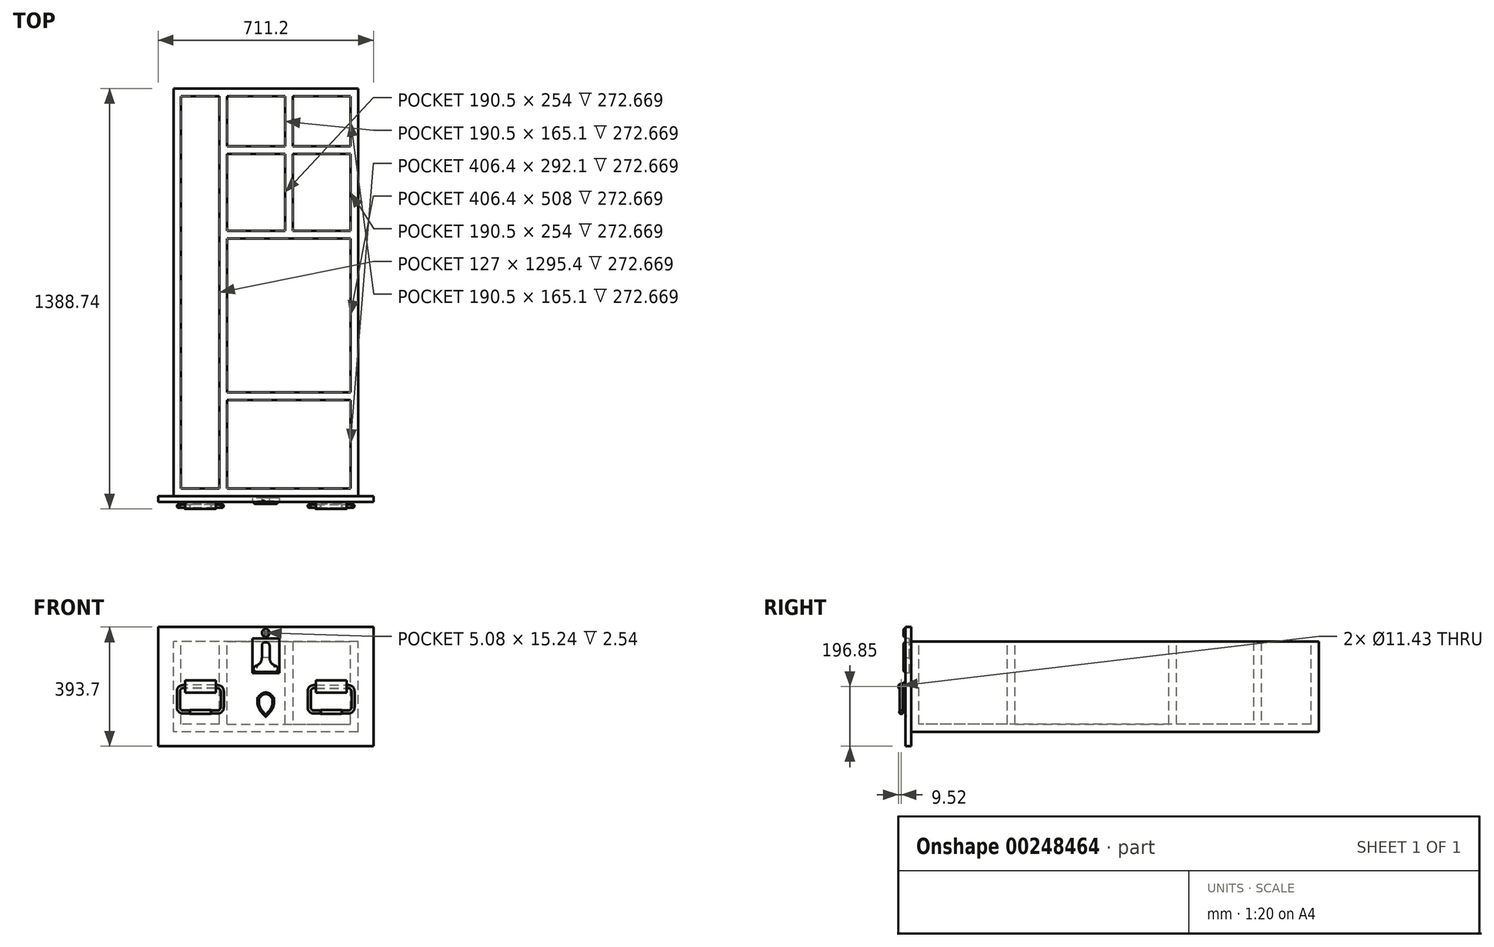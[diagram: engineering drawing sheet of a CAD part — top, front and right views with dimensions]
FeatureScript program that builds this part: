
annotation { "Feature Type Name" : "Feature", "Feature Type Description" : "" }
export const myFeature = defineFeature(function(context is Context, id is Id, definition is map)
    precondition{}
    {
        {
            var Q0;
            Q0=qCreatedBy(makeId("Front.planeOp"),FACE);
            var sketch = newSketch(context, id + "F0", { "sketchPlane" : qUnion([Q0])});
            skLineSegment(sketch, "E0.bottom", {"start": v(304.8, -149.03) * mm, "end": v(-304.8, -149.03) * mm});
            skLineSegment(sketch, "E0.top", {"start": v(304.8, 149.03) * mm, "end": v(-304.8, 149.03) * mm});
            skLineSegment(sketch, "E0.left", {"start": v(304.8, -149.03) * mm, "end": v(304.8, 149.03) * mm});
            skLineSegment(sketch, "E0.right", {"start": v(-304.8, -149.03) * mm, "end": v(-304.8, 149.03) * mm});
            skPoint(sketch, "E0.middle", {"position": v(0, 0) * mm});
            skSolve(sketch);
        }
        {
            var Q0;
            Q0 = qSketchRegion(id + "F0", true);
            extrude(context, id + "F1", {"entities" : qUnion([Q0]), "endBound" : BoundingType.SYMMETRIC, "depth" : 1346.2 * mm});
        }
        {
            var Q0;
            Q0=makeQuery(id+"F1.opExtrude","SWEPT_FACE",FACE,{"disambiguationData":[OSD([sQuery(id+"F0.wireOp",EDGE,"E0.top")])]});
            shell(context, id + "F2", {"entities" : qUnion([Q0]), "thickness" : 25.4 * mm});
        }
        {
            var Q0;
            Q0=makeQuery(id+"F1.opExtrude","CAP_FACE",FACE,{"disambiguationData":[OSD([sQuery(id+"F0.wireOp",EDGE,"E0.bottom"),sQuery(id+"F0.wireOp",EDGE,"E0.top"),sQuery(id+"F0.wireOp",EDGE,"E0.left"),sQuery(id+"F0.wireOp",EDGE,"E0.right")])],"isStart":false});
            var sketch = newSketch(context, id + "F3", { "sketchPlane" : qUnion([Q0])});
            skLineSegment(sketch, "E1.bottom", {"start": v(355.6, -196.85) * mm, "end": v(-355.6, -196.85) * mm});
            skLineSegment(sketch, "E1.top", {"start": v(355.6, 196.85) * mm, "end": v(-355.6, 196.85) * mm});
            skLineSegment(sketch, "E1.left", {"start": v(355.6, -196.85) * mm, "end": v(355.6, 196.85) * mm});
            skLineSegment(sketch, "E1.right", {"start": v(-355.6, -196.85) * mm, "end": v(-355.6, 196.85) * mm});
            skPoint(sketch, "E1.middle", {"position": v(0, 0) * mm});
            skSolve(sketch);
        }
        {
            var Q0;
            Q0 = qSketchRegion(id + "F3", true);
            extrude(context, id + "F4", {"entities" : qUnion([Q0]), "operationType" : NewBodyOperationType.ADD, "depth" : 19.05 * mm});
        }
        {
            var Q0;
            Q0=makeQuery(id+"F4.opExtrude","CAP_FACE",FACE,{"disambiguationData":[OSD([sQuery(id+"F3.wireOp",EDGE,"E1.bottom"),sQuery(id+"F3.wireOp",EDGE,"E1.top"),sQuery(id+"F3.wireOp",EDGE,"E1.left"),sQuery(id+"F3.wireOp",EDGE,"E1.right")])],"isStart":false});
            var sketch = newSketch(context, id + "F5", { "sketchPlane" : qUnion([Q0])});
            skLineSegment(sketch, "E2.bottom", {"start": v(44.45, 44.45) * mm, "end": v(-44.45, 44.45) * mm});
            skLineSegment(sketch, "E2.top", {"start": v(44.45, 158.75) * mm, "end": v(-44.45, 158.75) * mm});
            skLineSegment(sketch, "E2.left", {"start": v(44.45, 44.45) * mm, "end": v(44.45, 158.75) * mm});
            skLineSegment(sketch, "E2.right", {"start": v(-44.45, 44.45) * mm, "end": v(-44.45, 158.75) * mm});
            skPoint(sketch, "E2.middle", {"position": v(0, 101.6) * mm});
            skSolve(sketch);
        }
        {
            var Q0;
            Q0 = qSketchRegion(id + "F5", true);
            extrude(context, id + "F6", {"entities" : qUnion([Q0]), "operationType" : NewBodyOperationType.REMOVE, "oppositeDirection" : true, "depth" : 12.7 * mm});
        }
        {
            var Q0;
            Q0=makeQuery(id+"F6.boolean.opBoolean","COPY",FACE,{"derivedFrom":makeQuery(id+"F6.opExtrude","CAP_FACE",FACE,{"disambiguationData":[OSD([sQuery(id+"F5.wireOp",EDGE,"E2.bottom"),sQuery(id+"F5.wireOp",EDGE,"E2.top"),sQuery(id+"F5.wireOp",EDGE,"E2.left"),sQuery(id+"F5.wireOp",EDGE,"E2.right")])],"isStart":false})});
            var sketch = newSketch(context, id + "F7", { "sketchPlane" : qUnion([Q0])});
            skLineSegment(sketch, "E3.bottom", {"start": v(12.7, 95.25) * mm, "end": v(-12.7, 95.25) * mm});
            skLineSegment(sketch, "E3.top", {"start": v(2.54, 146.05) * mm, "end": v(-2.54, 146.05) * mm});
            skLineSegment(sketch, "E3.left", {"start": v(12.7, 95.25) * mm, "end": v(12.7, 135.9) * mm});
            skLineSegment(sketch, "E3.right", {"start": v(-12.7, 95.25) * mm, "end": v(-12.7, 135.9) * mm});
            skPoint(sketch, "E3.middle", {"position": v(0, 120.65) * mm});
            skPoint(sketch, "E3.middle.positionSnap0", {"position": v(0, 44.45) * mm});
            skPoint(sketch, "E3.centerSnap0", {"position": v(0, 44.45) * mm});
            skPoint(sketch, "E4.visualSharp", {"position": v(-12.7, 146.05) * mm});
            skArc(sketch, "E4.filletArc", {"start": v(-2.54, 146.05) * mm, "mid": v(-9.72, 143.07) * mm, "end": v(-12.7, 135.9) * mm});
            skPoint(sketch, "E5.visualSharp", {"position": v(12.7, 146.05) * mm});
            skArc(sketch, "E5.filletArc", {"start": v(12.7, 135.9) * mm, "mid": v(9.72, 143.07) * mm, "end": v(2.54, 146.05) * mm});
            skSolve(sketch);
        }
        {
            var Q0;
            Q0 = qSketchRegion(id + "F7", true);
            extrude(context, id + "F8", {"entities" : qUnion([Q0]), "operationType" : NewBodyOperationType.ADD, "depth" : 12.7 * mm});
        }
        {
            var Q0;
            Q0=makeQuery(id+"F8.opExtrude","CAP_FACE",FACE,{"disambiguationData":[OSD([sQuery(id+"F7.wireOp",EDGE,"E3.bottom"),sQuery(id+"F7.wireOp",EDGE,"E3.top"),sQuery(id+"F7.wireOp",EDGE,"E3.left"),sQuery(id+"F7.wireOp",EDGE,"E3.right"),sQuery(id+"F7.wireOp",EDGE,"E4.filletArc"),sQuery(id+"F7.wireOp",EDGE,"E5.filletArc")])],"isStart":false});
            var sketch = newSketch(context, id + "F9", { "sketchPlane" : qUnion([Q0])});
            skArc(sketch, "E6.0", {"start": v(-2.54, 146.05) * mm, "mid": v(-9.72, 143.07) * mm, "end": v(-12.7, 135.9) * mm});
            skLineSegment(sketch, "E6.1", {"start": v(12.7, 95.25) * mm, "end": v(12.7, 135.9) * mm});
            skLineSegment(sketch, "E6.2", {"start": v(2.54, 146.05) * mm, "end": v(-2.54, 146.05) * mm});
            skArc(sketch, "E6.3", {"start": v(12.7, 135.9) * mm, "mid": v(9.72, 143.07) * mm, "end": v(2.54, 146.05) * mm});
            skLineSegment(sketch, "E6.4", {"start": v(-12.7, 95.25) * mm, "end": v(-12.7, 135.9) * mm});
            skArc(sketch, "E7", {"start": v(-12.7, 95.25) * mm, "mid": v(-17.43, 79.6) * mm, "end": v(-30.05, 69.19) * mm});
            skLineSegment(sketch, "E8", {"start": v(0, 0) * mm, "end": v(0, 117.9) * mm, "construction": true});
            skArc(sketch, "E9", {"start": v(-30.05, 69.19) * mm, "mid": v(-40.18, 59.06) * mm, "end": v(-30.05, 48.93) * mm});
            skLineSegment(sketch, "E10", {"start": v(-30.05, 48.93) * mm, "end": v(0, 48.93) * mm});
            skLineSegment(sketch, "E11.MirrorCS", {"start": v(30.05, 48.93) * mm, "end": v(0, 48.93) * mm});
            skArc(sketch, "E12.MirrorCS", {"start": v(30.05, 69.19) * mm, "mid": v(40.18, 59.06) * mm, "end": v(30.05, 48.93) * mm});
            skArc(sketch, "E13.MirrorCS", {"start": v(12.7, 95.25) * mm, "mid": v(17.43, 79.6) * mm, "end": v(30.05, 69.19) * mm});
            skSolve(sketch);
        }
        {
            var Q0;
            Q0 = qSketchRegion(id + "F9", true);
            extrude(context, id + "F10", {"entities" : qUnion([Q0]), "operationType" : NewBodyOperationType.ADD, "depth" : 6.35 * mm});
        }
        {
            var Q0;
            Q0=makeQuery(id+"F10.opExtrude","CAP_FACE",FACE,{"disambiguationData":[OSD([sQuery(id+"F9.wireOp",EDGE,"E6.0"),sQuery(id+"F9.wireOp",EDGE,"E6.1"),sQuery(id+"F9.wireOp",EDGE,"E6.2"),sQuery(id+"F9.wireOp",EDGE,"E6.3"),sQuery(id+"F9.wireOp",EDGE,"E6.4"),sQuery(id+"F9.wireOp",EDGE,"E7"),sQuery(id+"F9.wireOp",EDGE,"E9"),sQuery(id+"F9.wireOp",EDGE,"E10"),sQuery(id+"F9.wireOp",EDGE,"E11.MirrorCS"),sQuery(id+"F9.wireOp",EDGE,"E12.MirrorCS"),sQuery(id+"F9.wireOp",EDGE,"E13.MirrorCS")])],"isStart":false});
            fillet(context, id + "F11", {"entities" : qUnion([Q0]), "radius" : 5.08 * mm, "tangentPropagation" : true, "allowEdgeOverflow" : false});
        }
        {
            var Q0;
            Q0=makeQuery(id+"F4.opExtrude","CAP_FACE",FACE,{"disambiguationData":[OSD([sQuery(id+"F3.wireOp",EDGE,"E1.bottom"),sQuery(id+"F3.wireOp",EDGE,"E1.top"),sQuery(id+"F3.wireOp",EDGE,"E1.left"),sQuery(id+"F3.wireOp",EDGE,"E1.right")])],"isStart":false});
            var sketch = newSketch(context, id + "F12", { "sketchPlane" : qUnion([Q0])});
            skCircle(sketch, "E14", {"center": v(0, 177.8) * mm, "radius": 12.7 * mm});
            skPoint(sketch, "E14.centerSnap0", {"position": v(0, 158.75) * mm});
            skSolve(sketch);
        }
        {
            var Q0;
            Q0 = qSketchRegion(id + "F12", true);
            extrude(context, id + "F13", {"entities" : qUnion([Q0]), "operationType" : NewBodyOperationType.ADD, "depth" : 6.35 * mm});
        }
        {
            var Q0;
            Q0=makeQuery(id+"F13.opExtrude","CAP_FACE",FACE,{"disambiguationData":[OSD([sQuery(id+"F12.wireOp",EDGE,"E14")])],"isStart":false});
            fillet(context, id + "F14", {"entities" : qUnion([Q0]), "radius" : 2.54 * mm, "tangentPropagation" : true, "allowEdgeOverflow" : false});
        }
        {
            var Q0;
            Q0=makeQuery(id+"F13.opExtrude","CAP_FACE",FACE,{"disambiguationData":[OSD([sQuery(id+"F12.wireOp",EDGE,"E14")])],"isStart":false});
            var sketch = newSketch(context, id + "F15", { "sketchPlane" : qUnion([Q0])});
            skLineSegment(sketch, "E15.bottom", {"start": v(2.54, 170.18) * mm, "end": v(-2.54, 170.18) * mm});
            skLineSegment(sketch, "E15.top", {"start": v(2.54, 185.42) * mm, "end": v(-2.54, 185.42) * mm});
            skLineSegment(sketch, "E15.left", {"start": v(2.54, 170.18) * mm, "end": v(2.54, 185.42) * mm});
            skLineSegment(sketch, "E15.right", {"start": v(-2.54, 170.18) * mm, "end": v(-2.54, 185.42) * mm});
            skPoint(sketch, "E15.middle", {"position": v(0, 177.8) * mm});
            skSolve(sketch);
        }
        {
            var Q0;
            Q0 = qSketchRegion(id + "F15", true);
            extrude(context, id + "F16", {"entities" : qUnion([Q0]), "operationType" : NewBodyOperationType.REMOVE, "oppositeDirection" : true, "depth" : 2.54 * mm});
        }
        {
            var Q0;
            Q0=makeQuery(id+"F4.opExtrude","SWEPT_FACE",FACE,{"disambiguationData":[OSD([sQuery(id+"F3.wireOp",EDGE,"E1.left")])]});
            var Q1;
            Q1=makeQuery(id+"F4.opExtrude","SWEPT_FACE",FACE,{"disambiguationData":[OSD([sQuery(id+"F3.wireOp",EDGE,"E1.right")])]});
            cPlane(context, id + "F17", {"entities" : qUnion([Q0, Q1]), "cplaneType" : CPlaneType.MID_PLANE, "offset" : 25.4 * mm, "width" : 152.4 * mm, "height" : 152.4 * mm});
        }
        {
            var Q0;
            Q0=qCreatedBy(id+"F17.planeOp",FACE);
            var Q1;
            Q1=makeQuery(id+"F4.opExtrude","SWEPT_FACE",FACE,{"disambiguationData":[OSD([sQuery(id+"F3.wireOp",EDGE,"E1.right")])]});
            cPlane(context, id + "F18", {"entities" : qUnion([Q0, Q1]), "cplaneType" : CPlaneType.MID_PLANE, "offset" : 25.4 * mm, "width" : 152.4 * mm, "height" : 152.4 * mm});
        }
        {
            var Q0;
            Q0=qCreatedBy(id+"F18.planeOp",FACE);
            cPlane(context, id + "F19", {"entities" : qUnion([Q0]), "cplaneType" : CPlaneType.OFFSET, "offset" : 38.1 * mm, "oppositeDirection" : true, "width" : 152.4 * mm, "height" : 152.4 * mm});
        }
        {
            var Q0;
            Q0=qCreatedBy(id+"F19.planeOp",FACE);
            var sketch = newSketch(context, id + "F20", { "sketchPlane" : qUnion([Q0])});
            skLineSegment(sketch, "E16", {"start": v(-712.13, 0) * mm, "end": v(-955.12, 0) * mm, "construction": true});
            skCircle(sketch, "E17", {"center": v(-706.12, 0) * mm, "radius": 9.53 * mm});
            skCircle(sketch, "E18", {"center": v(-706.12, 0) * mm, "radius": 5.72 * mm});
            skArc(sketch, "E19", {"start": v(-706.7, 9.5) * mm, "mid": v(-697.79, 12.77) * mm, "end": v(-692.15, 20.4) * mm});
            skArc(sketch, "E20.MirrorCS", {"start": v(-706.7, -9.5) * mm, "mid": v(-697.79, -12.77) * mm, "end": v(-692.15, -20.4) * mm});
            skLineSegment(sketch, "E21", {"start": v(-692.15, 20.4) * mm, "end": v(-692.15, -20.4) * mm});
            skSolve(sketch);
        }
        {
            var Q0;
            Q0 = qSketchRegion(id + "F20", true);
            extrude(context, id + "F21", {"entities" : qUnion([Q0]), "endBound" : BoundingType.SYMMETRIC, "depth" : 101.6 * mm});
        }
        {
            var Q0;
            Q0=makeQuery(id+"F21.opExtrude","SWEPT_BODY",BODY,{"disambiguationData":[OSD([sQuery(id+"F20.wireOp",EDGE,"E17"),sQuery(id+"F20.wireOp",EDGE,"E18"),sQuery(id+"F20.wireOp",EDGE,"E19"),sQuery(id+"F20.wireOp",EDGE,"E20.MirrorCS"),sQuery(id+"F20.wireOp",EDGE,"E21")])]});
            var Q1;
            Q1=qCreatedBy(id+"F17.planeOp",FACE);
            mirror(context, id + "F22", {"entities" : qUnion([Q0]), "mirrorPlane" : qUnion([Q1])});
        }
        {
            var Q0;
            Q0=makeQuery(id+"F4.opExtrude","CAP_FACE",FACE,{"disambiguationData":[OSD([sQuery(id+"F3.wireOp",EDGE,"E1.bottom"),sQuery(id+"F3.wireOp",EDGE,"E1.top"),sQuery(id+"F3.wireOp",EDGE,"E1.left"),sQuery(id+"F3.wireOp",EDGE,"E1.right")])],"isStart":false});
            cPlane(context, id + "F23", {"entities" : qUnion([Q0]), "cplaneType" : CPlaneType.OFFSET, "offset" : 13.97 * mm, "width" : 152.4 * mm, "height" : 152.4 * mm});
        }
        {
            var Q0;
            Q0=qCreatedBy(id+"F23.planeOp",FACE);
            var sketch = newSketch(context, id + "F24", { "sketchPlane" : qUnion([Q0])});
            skLineSegment(sketch, "E22", {"start": v(-165.1, 0) * mm, "end": v(-266.7, 0) * mm});
            skLineSegment(sketch, "E23", {"start": v(-215.9, 0) * mm, "end": v(-215.9, 15.8) * mm, "construction": true});
            skLineSegment(sketch, "E24", {"start": v(-165.1, 0) * mm, "end": v(-158.75, 0) * mm});
            skArc(sketch, "E25", {"start": v(-158.75, 0) * mm, "mid": v(-147.97, -4.46) * mm, "end": v(-143.5, -15.24) * mm});
            skLineSegment(sketch, "E26", {"start": v(-143.5, -15.24) * mm, "end": v(-143.5, -68.58) * mm});
            skLineSegment(sketch, "E27", {"start": v(-143.5, -41.91) * mm, "end": v(-163.62, -41.91) * mm, "construction": true});
            skArc(sketch, "E28.MirrorCS", {"start": v(-158.75, -83.82) * mm, "mid": v(-147.97, -79.36) * mm, "end": v(-143.5, -68.58) * mm});
            skLineSegment(sketch, "E29.MirrorCS", {"start": v(-266.7, 0) * mm, "end": v(-273.05, 0) * mm});
            skArc(sketch, "E30.MirrorCS", {"start": v(-273.05, 0) * mm, "mid": v(-283.83, -4.46) * mm, "end": v(-288.29, -15.24) * mm});
            skLineSegment(sketch, "E31.MirrorCS", {"start": v(-288.3, -15.24) * mm, "end": v(-288.3, -68.58) * mm});
            skArc(sketch, "E32.MirrorCS", {"start": v(-273.05, -83.82) * mm, "mid": v(-283.83, -79.36) * mm, "end": v(-288.29, -68.58) * mm});
            skLineSegment(sketch, "E33", {"start": v(-273.05, -83.82) * mm, "end": v(-158.75, -83.82) * mm});
            skSolve(sketch);
        }
        {
            var Q0;
            Q0=makeQuery(id+"F21.opExtrude","CAP_FACE",FACE,{"disambiguationData":[OSD([sQuery(id+"F20.wireOp",EDGE,"E17"),sQuery(id+"F20.wireOp",EDGE,"E18"),sQuery(id+"F20.wireOp",EDGE,"E19"),sQuery(id+"F20.wireOp",EDGE,"E20.MirrorCS"),sQuery(id+"F20.wireOp",EDGE,"E21")])],"isStart":true});
            var sketch = newSketch(context, id + "F25", { "sketchPlane" : qUnion([Q0])});
            skCircle(sketch, "E34", {"center": v(706.12, 0) * mm, "radius": 5.08 * mm});
            skSolve(sketch);
        }
        {
            var Q0;
            Q0 = qSketchRegion(id + "F25", true);
            var Q1;
            Q1 = qBodyType(qCreatedBy(id + "F24" ,EDGE), BodyType.WIRE);
            sweep(context, id + "F26", {"profiles" : qUnion([Q0]), "path" : qUnion([Q1])});
        }
        {
            var Q0;
            Q0=qCreatedBy(id+"F23.planeOp",FACE);
            var sketch = newSketch(context, id + "F27", { "sketchPlane" : qUnion([Q0])});
            skLineSegment(sketch, "E35", {"start": v(-215.9, -83.82) * mm, "end": v(-215.9, -54.84) * mm, "construction": true});
            skLineSegment(sketch, "E36", {"start": v(-215.9, -83.82) * mm, "end": v(-180.34, -83.82) * mm});
            skLineSegment(sketch, "E37.MirrorCS", {"start": v(-215.9, -83.82) * mm, "end": v(-251.46, -83.82) * mm});
            skSolve(sketch);
        }
        {
            var Q0;
            Q0=qCreatedBy(id+"F17.planeOp",FACE);
            var Q1;
            Q1=sQuery(id+"F27.wireOp",VERTEX,"E37.MirrorCS.end");
            cPlane(context, id + "F28", {"entities" : qUnion([Q0, Q1]), "cplaneType" : CPlaneType.PLANE_POINT, "offset" : 25.4 * mm, "width" : 152.4 * mm, "height" : 152.4 * mm});
        }
        {
            var Q0;
            Q0=qCreatedBy(id+"F28.planeOp",FACE);
            var sketch = newSketch(context, id + "F29", { "sketchPlane" : qUnion([Q0])});
            skCircle(sketch, "E38", {"center": v(-706.12, -83.82) * mm, "radius": 6.35 * mm});
            skSolve(sketch);
        }
        {
            var Q0;
            Q0 = qSketchRegion(id + "F29", true);
            var Q1;
            Q1 = qBodyType(qCreatedBy(id + "F27" ,EDGE), BodyType.WIRE);
            sweep(context, id + "F30", {"operationType" : NewBodyOperationType.ADD, "profiles" : qUnion([Q0]), "path" : qUnion([Q1])});
        }
        {
            var Q0;
            Q0=makeQuery(id+"F30.opSweep","CAP_EDGE",EDGE,{"disambiguationData":[OSD([sQuery(id+"F27.wireOp",VERTEX,"E37.MirrorCS.end"),sQuery(id+"F29.wireOp",EDGE,"E38")])],"isStart":true});
            var Q1;
            Q1=makeQuery(id+"F30.opSweep","CAP_EDGE",EDGE,{"disambiguationData":[OSD([sQuery(id+"F27.wireOp",VERTEX,"E36.end"),sQuery(id+"F29.wireOp",EDGE,"E38")])],"isStart":false});
            chamfer(context, id + "F31", {"entities" : qUnion([Q0, Q1]), "width" : 1.27 * mm, "tangentPropagation" : true});
        }
        {
            var Q0;
            Q0=makeQuery(id+"F26.opSweep","SWEPT_BODY",BODY,{"disambiguationData":[OSD([sQuery(id+"F24.wireOp",EDGE,"E24"),sQuery(id+"F25.wireOp",EDGE,"E34")])]});
            var Q1;
            Q1=qCreatedBy(id+"F17.planeOp",FACE);
            mirror(context, id + "F32", {"entities" : qUnion([Q0]), "mirrorPlane" : qUnion([Q1])});
        }
        {
            var Q0;
            Q0=makeQuery(id+"F1.opExtrude","SWEPT_FACE",FACE,{"disambiguationData":[OSD([sQuery(id+"F0.wireOp",EDGE,"E0.top")])]});
            var sketch = newSketch(context, id + "F33", { "sketchPlane" : qUnion([Q0])});
            skLineSegment(sketch, "E39.bottom", {"start": v(-152.4, 647.7) * mm, "end": v(-127, 647.7) * mm});
            skLineSegment(sketch, "E39.top", {"start": v(-152.4, -647.7) * mm, "end": v(-127, -647.7) * mm});
            skLineSegment(sketch, "E39.left", {"start": v(-152.4, 647.7) * mm, "end": v(-152.4, -647.7) * mm});
            skLineSegment(sketch, "E39.right", {"start": v(-127, 647.7) * mm, "end": v(-127, -647.7) * mm});
            skSolve(sketch);
        }
        {
            var Q0;
            Q0 = qSketchRegion(id + "F33", true);
            var Q1;
            Q1=makeQuery(id+"F2.opShell","OFFSET_FACE",FACE,{"disambiguationData":[OSD([sQuery(id+"F0.wireOp",EDGE,"E0.bottom")])]});
            extrude(context, id + "F34", {"entities" : qUnion([Q0]), "operationType" : NewBodyOperationType.ADD, "endBound" : BoundingType.UP_TO_SURFACE, "oppositeDirection" : true, "endBoundEntityFace" : qUnion([Q1]), "depth" : 25.4 * mm});
        }
        {
            var Q0;
            Q0=makeQuery(id+"F34.boolean.opBoolean","MERGE",FACE,{"derivedFrom":[makeQuery(id+"F1.opExtrude","SWEPT_FACE",FACE,{"disambiguationData":[OSD([sQuery(id+"F0.wireOp",EDGE,"E0.top")])]}),makeQuery(id+"F34.opExtrude","CAP_FACE",FACE,{"disambiguationData":[OSD([sQuery(id+"F33.wireOp",EDGE,"E39.bottom"),sQuery(id+"F33.wireOp",EDGE,"E39.top"),sQuery(id+"F33.wireOp",EDGE,"E39.left"),sQuery(id+"F33.wireOp",EDGE,"E39.right")])],"isStart":true})]});
            var sketch = newSketch(context, id + "F35", { "sketchPlane" : qUnion([Q0])});
            skLineSegment(sketch, "E40.bottom", {"start": v(-127, 482.6) * mm, "end": v(279.4, 482.6) * mm});
            skLineSegment(sketch, "E40.top", {"start": v(-127, 457.2) * mm, "end": v(279.4, 457.2) * mm});
            skLineSegment(sketch, "E40.left", {"start": v(-127, 482.6) * mm, "end": v(-127, 457.2) * mm});
            skLineSegment(sketch, "E40.right", {"start": v(279.4, 482.6) * mm, "end": v(279.4, 457.2) * mm});
            skLineSegment(sketch, "E41.bottom", {"start": v(-127, 203.2) * mm, "end": v(279.4, 203.2) * mm});
            skLineSegment(sketch, "E41.top", {"start": v(-127, 177.8) * mm, "end": v(279.4, 177.8) * mm});
            skLineSegment(sketch, "E41.left", {"start": v(-127, 203.2) * mm, "end": v(-127, 177.8) * mm});
            skLineSegment(sketch, "E41.right", {"start": v(279.4, 203.2) * mm, "end": v(279.4, 177.8) * mm});
            skLineSegment(sketch, "E42.bottom", {"start": v(-127, -330.2) * mm, "end": v(279.4, -330.2) * mm});
            skLineSegment(sketch, "E42.top", {"start": v(-127, -355.6) * mm, "end": v(279.4, -355.6) * mm});
            skLineSegment(sketch, "E42.left", {"start": v(-127, -330.2) * mm, "end": v(-127, -355.6) * mm});
            skLineSegment(sketch, "E42.right", {"start": v(279.4, -330.2) * mm, "end": v(279.4, -355.6) * mm});
            skSolve(sketch);
        }
        {
            var Q0;
            Q0 = qSketchRegion(id + "F35", true);
            var Q1;
            {var subQ1=sQuery(id+"F0.wireOp",EDGE,"E0.left");var subQ3=sQuery(id+"F0.wireOp",EDGE,"E0.bottom");Q1=makeQuery(id+"F34.boolean.opBoolean","SPLIT",FACE,{"disambiguationData":[TD([makeQuery(id+"F2.opShell","OFFSET_FACE",FACE,{"disambiguationData":[OSD([subQ1])]})])],"derivedFrom":makeQuery(id+"F2.opShell","OFFSET_FACE",FACE,{"disambiguationData":[OSD([subQ3])]})});}
            extrude(context, id + "F36", {"entities" : qUnion([Q0]), "operationType" : NewBodyOperationType.ADD, "endBound" : BoundingType.UP_TO_SURFACE, "oppositeDirection" : true, "endBoundEntityFace" : qUnion([Q1]), "depth" : 25.4 * mm});
        }
        {
            var Q0;
            Q0=makeQuery(id+"F36.boolean.opBoolean","MERGE",FACE,{"derivedFrom":[makeQuery(id+"F34.boolean.opBoolean","MERGE",FACE,{"derivedFrom":[makeQuery(id+"F1.opExtrude","SWEPT_FACE",FACE,{"disambiguationData":[OSD([sQuery(id+"F0.wireOp",EDGE,"E0.top")])]}),makeQuery(id+"F34.opExtrude","CAP_FACE",FACE,{"disambiguationData":[OSD([sQuery(id+"F33.wireOp",EDGE,"E39.bottom"),sQuery(id+"F33.wireOp",EDGE,"E39.top"),sQuery(id+"F33.wireOp",EDGE,"E39.left"),sQuery(id+"F33.wireOp",EDGE,"E39.right")])],"isStart":true})]}),makeQuery(id+"F36.opExtrude","CAP_FACE",FACE,{"disambiguationData":[OSD([sQuery(id+"F35.wireOp",EDGE,"E40.bottom"),sQuery(id+"F35.wireOp",EDGE,"E40.top"),sQuery(id+"F35.wireOp",EDGE,"E40.left"),sQuery(id+"F35.wireOp",EDGE,"E40.right")])],"isStart":true}),makeQuery(id+"F36.opExtrude","CAP_FACE",FACE,{"disambiguationData":[OSD([sQuery(id+"F35.wireOp",EDGE,"E41.bottom"),sQuery(id+"F35.wireOp",EDGE,"E41.top"),sQuery(id+"F35.wireOp",EDGE,"E41.left"),sQuery(id+"F35.wireOp",EDGE,"E41.right")])],"isStart":true}),makeQuery(id+"F36.opExtrude","CAP_FACE",FACE,{"disambiguationData":[OSD([sQuery(id+"F35.wireOp",EDGE,"E42.bottom"),sQuery(id+"F35.wireOp",EDGE,"E42.top"),sQuery(id+"F35.wireOp",EDGE,"E42.left"),sQuery(id+"F35.wireOp",EDGE,"E42.right")])],"isStart":true})]});
            var sketch = newSketch(context, id + "F37", { "sketchPlane" : qUnion([Q0])});
            skLineSegment(sketch, "E43", {"start": v(76.2, 647.7) * mm, "end": v(76.2, 121.25) * mm, "construction": true});
            skPoint(sketch, "E43.endSnap0", {"position": v(76.2, 457.2) * mm});
            skLineSegment(sketch, "E44.bottom", {"start": v(63.5, 647.7) * mm, "end": v(88.9, 647.7) * mm});
            skLineSegment(sketch, "E44.top", {"start": v(63.5, 203.2) * mm, "end": v(88.9, 203.2) * mm});
            skLineSegment(sketch, "E44.left", {"start": v(63.5, 647.7) * mm, "end": v(63.5, 203.2) * mm});
            skLineSegment(sketch, "E44.right", {"start": v(88.9, 647.7) * mm, "end": v(88.9, 203.2) * mm});
            skSolve(sketch);
        }
        {
            var Q0;
            Q0 = qSketchRegion(id + "F37", true);
            var Q1;
            {var subQ0=sQuery(id+"F0.wireOp",EDGE,"E0.left");var subQ1=makeQuery(id+"F2.opShell","OFFSET_FACE",FACE,{"disambiguationData":[OSD([subQ0])]});var subQ5=sQuery(id+"F0.wireOp",EDGE,"E0.bottom");Q1=makeQuery(id+"F36.boolean.opBoolean","SPLIT",FACE,{"disambiguationData":[TD([makeQuery(id+"F36.opExtrude","SWEPT_FACE",FACE,{"disambiguationData":[OSD([sQuery(id+"F35.wireOp",EDGE,"E40.top")])]})])],"derivedFrom":makeQuery(id+"F34.boolean.opBoolean","SPLIT",FACE,{"disambiguationData":[TD([subQ1])],"derivedFrom":makeQuery(id+"F2.opShell","OFFSET_FACE",FACE,{"disambiguationData":[OSD([subQ5])]})})});}
            extrude(context, id + "F38", {"entities" : qUnion([Q0]), "operationType" : NewBodyOperationType.ADD, "endBound" : BoundingType.UP_TO_SURFACE, "oppositeDirection" : true, "endBoundEntityFace" : qUnion([Q1]), "depth" : 25.4 * mm});
        }
        {
            var Q0;
            Q0=makeQuery(id+"F4.opExtrude","CAP_FACE",FACE,{"disambiguationData":[OSD([sQuery(id+"F3.wireOp",EDGE,"E1.bottom"),sQuery(id+"F3.wireOp",EDGE,"E1.top"),sQuery(id+"F3.wireOp",EDGE,"E1.left"),sQuery(id+"F3.wireOp",EDGE,"E1.right")])],"isStart":false});
            var sketch = newSketch(context, id + "F39", { "sketchPlane" : qUnion([Q0])});
            skLineSegment(sketch, "E45", {"start": v(0, -119.69) * mm, "end": v(0, 81.98) * mm, "construction": true});
            skFitSpline(sketch, "E46", {"points": [v(0, -99.66) * mm, v(-26.56, -35) * mm], "startDerivative": vector(-94.3, 90.63) * mm, "endDerivative": vector(5.61, 60.71) * mm});
            skFitSpline(sketch, "E47", {"points": [v(-26.56, -35) * mm, v(0, -18.85) * mm], "startDerivative": vector(26.56, 16.14) * mm, "endDerivative": vector(61.74, 11.54) * mm});
            skFitSpline(sketch, "E48.MirrorCS", {"points": [v(0, -99.66) * mm, v(26.56, -35) * mm], "startDerivative": vector(94.3, 90.63) * mm, "endDerivative": vector(-5.61, 60.71) * mm});
            skFitSpline(sketch, "E49.MirrorCS", {"points": [v(26.56, -35) * mm, v(0, -18.85) * mm], "startDerivative": vector(-26.56, 16.14) * mm, "endDerivative": vector(-61.74, 11.54) * mm});
            skFitSpline(sketch, "E50.0", {"points": [v(23.92, -39.34) * mm, v(23.24, -38.92) * mm, v(21.97, -38.07) * mm, v(20.33, -36.73) * mm, v(18.93, -35.39) * mm, v(17.74, -34.1) * mm, v(16.72, -32.9) * mm, v(15.81, -31.8) * mm, v(14.97, -30.84) * mm, v(14.14, -29.98) * mm, v(13.26, -29.18) * mm, v(12.26, -28.4) * mm, v(11.04, -27.64) * mm, v(9.02, -26.6) * mm, v(5.57, -25.28) * mm, v(1.5, -24.3) * mm, v(-0.93, -23.85) * mm]});
            skFitSpline(sketch, "E50.1", {"points": [v(-3.52, -96) * mm, v(0.32, -92.3) * mm, v(6.9, -85.45) * mm, v(13.91, -76.55) * mm, v(18.48, -68.84) * mm, v(21.14, -62.05) * mm, v(22.39, -55.77) * mm, v(22.65, -49.5) * mm, v(22.24, -42.88) * mm, v(21.74, -38.03) * mm, v(21.5, -35.46) * mm]});
            skFitSpline(sketch, "E50.2", {"points": [v(3.52, -96) * mm, v(-0.32, -92.3) * mm, v(-6.9, -85.45) * mm, v(-13.91, -76.55) * mm, v(-18.48, -68.84) * mm, v(-21.14, -62.05) * mm, v(-22.39, -55.77) * mm, v(-22.65, -49.5) * mm, v(-22.24, -42.88) * mm, v(-21.74, -38.03) * mm, v(-21.5, -35.46) * mm]});
            skFitSpline(sketch, "E50.3", {"points": [v(-23.92, -39.34) * mm, v(-23.24, -38.92) * mm, v(-21.97, -38.07) * mm, v(-20.33, -36.73) * mm, v(-18.93, -35.39) * mm, v(-17.74, -34.1) * mm, v(-16.72, -32.9) * mm, v(-15.81, -31.8) * mm, v(-14.97, -30.84) * mm, v(-14.14, -29.98) * mm, v(-13.26, -29.18) * mm, v(-12.26, -28.4) * mm, v(-11.04, -27.64) * mm, v(-9.02, -26.6) * mm, v(-5.57, -25.28) * mm, v(-1.5, -24.3) * mm, v(0.93, -23.85) * mm]});
            skLineSegment(sketch, "E51", {"start": v(4.83, -19.91) * mm, "end": v(4.83, -25.18) * mm});
            skLineSegment(sketch, "E52.MirrorCS", {"start": v(-4.83, -19.91) * mm, "end": v(-4.83, -25.18) * mm});
            skLineSegment(sketch, "E53.trimOffspring", {"start": v(4.83, -87.47) * mm, "end": v(4.83, -94.87) * mm});
            skLineSegment(sketch, "E54.trimOffspring", {"start": v(-4.83, -87.47) * mm, "end": v(-4.83, -94.87) * mm});
            skText(sketch, "E55", { "text": "OD", "fontName": "AllertaStencil-Regular.ttf"});
            skText(sketch, "E56", { "text": "W", "fontName": "AllertaStencil-Regular.ttf"});
            skLineSegment(sketch, "E57", {"start": v(-22.85, -57.4) * mm, "end": v(116.85, -57.4) * mm, "construction": true});
            const initialGuessF39  = {"E55": [-0.01742, -0.05412, 1, 0, 0.01682], "E56": [-0.01143, -0.07505, 1, 0, 0.01545]};
            skSetInitialGuess(sketch, initialGuessF39);
            skSolve(sketch);
        }
        {
            var Q0;
            Q0 = qSketchRegion(id + "F39", true);
            extrude(context, id + "F40", {"entities" : qUnion([Q0]), "operationType" : NewBodyOperationType.REMOVE, "oppositeDirection" : true, "depth" : 2.54 * mm});
        }
    });
